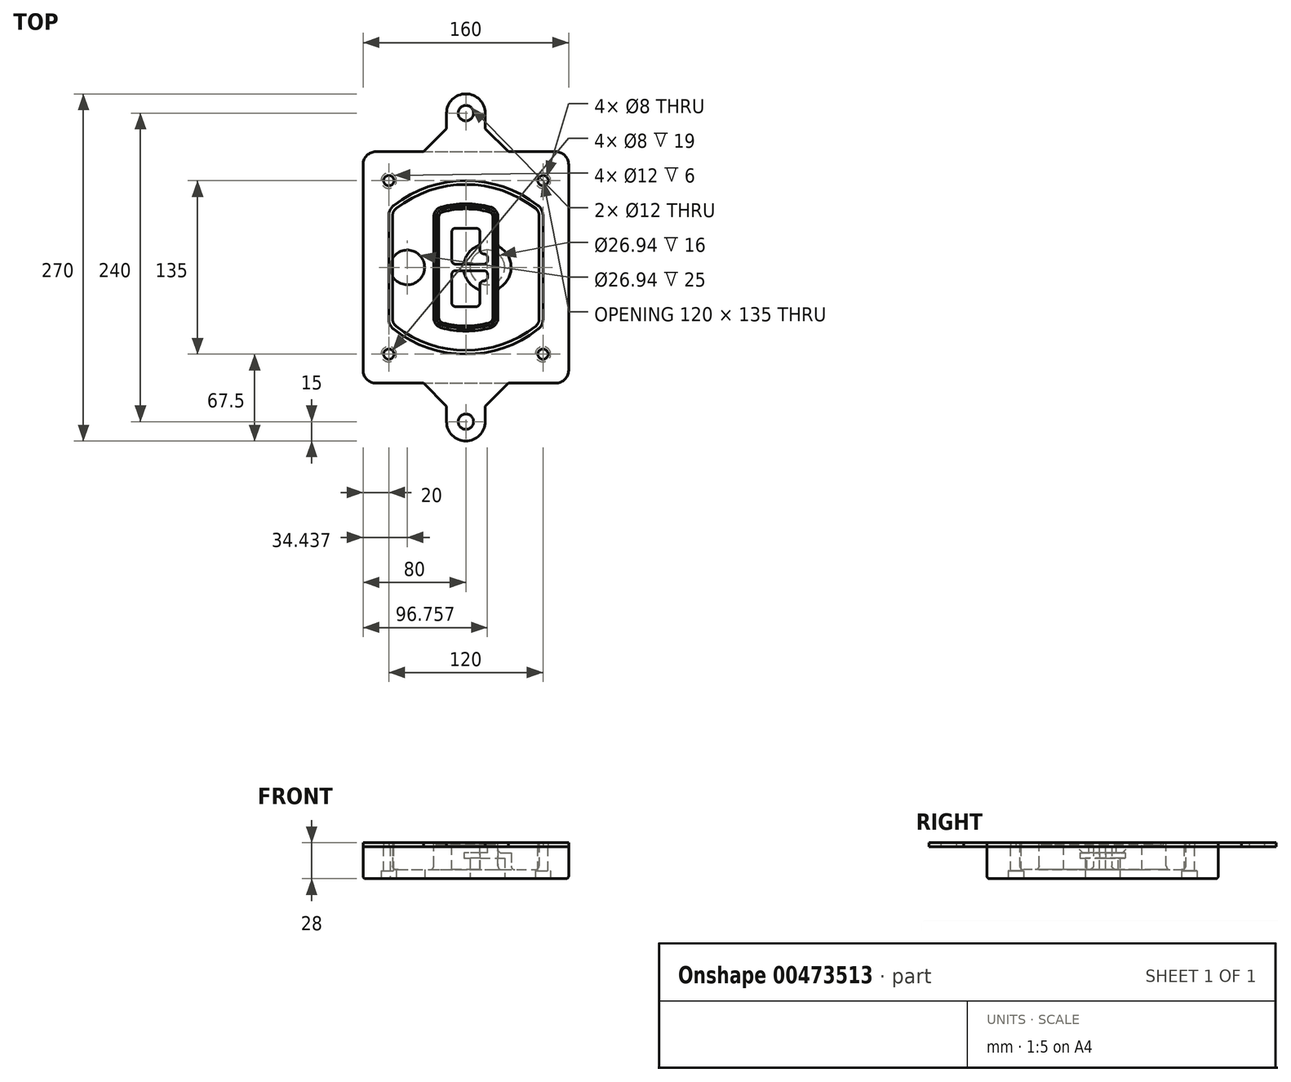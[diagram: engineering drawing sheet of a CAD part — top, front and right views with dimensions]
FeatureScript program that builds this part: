
annotation { "Feature Type Name" : "Feature", "Feature Type Description" : "" }
export const myFeature = defineFeature(function(context is Context, id is Id, definition is map)
    precondition{}
    {
        {
            var Q0;
            Q0=qCreatedBy(makeId("Top.planeOp"),FACE);
            var sketch = newSketch(context, id + "F0", { "sketchPlane" : qUnion([Q0])});
            skPoint(sketch, "E0.rect.middle", {"position": v(0, 0) * mm});
            skLineSegment(sketch, "E1.bottom", {"start": v(-70, -90) * mm, "end": v(70, -90) * mm});
            skLineSegment(sketch, "E1.top", {"start": v(-70, 90) * mm, "end": v(70, 90) * mm});
            skLineSegment(sketch, "E1.left", {"start": v(-80, -80) * mm, "end": v(-80, 80) * mm});
            skLineSegment(sketch, "E1.right", {"start": v(80, -80) * mm, "end": v(80, 80) * mm});
            skLineSegment(sketch, "E2", {"start": v(-80, 90) * mm, "end": v(80, -90) * mm, "construction": true});
            skLineSegment(sketch, "E3", {"start": v(80, 90) * mm, "end": v(-80, -90) * mm, "construction": true});
            skCircle(sketch, "E4", {"center": v(-60, 67.5) * mm, "radius": 4 * mm});
            skCircle(sketch, "E5", {"center": v(60, 67.5) * mm, "radius": 4 * mm});
            skCircle(sketch, "E6", {"center": v(60, -67.5) * mm, "radius": 4 * mm});
            skCircle(sketch, "E7", {"center": v(-60, -67.5) * mm, "radius": 4 * mm});
            skLineSegment(sketch, "E8", {"start": v(-60, 67.5) * mm, "end": v(60, 67.5) * mm, "construction": true});
            skLineSegment(sketch, "E9", {"start": v(60, 67.5) * mm, "end": v(60, -67.5) * mm, "construction": true});
            skLineSegment(sketch, "E10", {"start": v(60, -67.5) * mm, "end": v(-60, -67.5) * mm, "construction": true});
            skLineSegment(sketch, "E11", {"start": v(-60, -67.5) * mm, "end": v(-60, 67.5) * mm, "construction": true});
            skLineSegment(sketch, "E12", {"start": v(-60, 40.3) * mm, "end": v(-60, -40.3) * mm});
            skLineSegment(sketch, "E13", {"start": v(60, 40.3) * mm, "end": v(60, -40.3) * mm});
            skArc(sketch, "E14", {"start": v(56.15, 48.18) * mm, "mid": v(0, 67.5) * mm, "end": v(-56.15, 48.18) * mm});
            skArc(sketch, "E15", {"start": v(-56.15, -48.18) * mm, "mid": v(0, -67.5) * mm, "end": v(56.15, -48.18) * mm});
            skLineSegment(sketch, "E16", {"start": v(-60, 0) * mm, "end": v(60, 0) * mm, "construction": true});
            skPoint(sketch, "E17.visualSharp", {"position": v(-60, -45) * mm});
            skArc(sketch, "E17.filletArc", {"start": v(-60, -40.3) * mm, "mid": v(-58.99, -44.68) * mm, "end": v(-56.15, -48.18) * mm});
            skPoint(sketch, "E18.visualSharp", {"position": v(-60, 45) * mm});
            skArc(sketch, "E18.filletArc", {"start": v(-56.15, 48.18) * mm, "mid": v(-58.99, 44.68) * mm, "end": v(-60, 40.3) * mm});
            skPoint(sketch, "E19.visualSharp", {"position": v(60, 45) * mm});
            skArc(sketch, "E19.filletArc", {"start": v(60, 40.3) * mm, "mid": v(58.99, 44.68) * mm, "end": v(56.15, 48.18) * mm});
            skPoint(sketch, "E20.visualSharp", {"position": v(60, -45) * mm});
            skArc(sketch, "E20.filletArc", {"start": v(56.15, -48.18) * mm, "mid": v(58.99, -44.68) * mm, "end": v(60, -40.3) * mm});
            skPoint(sketch, "E21.visualSharp", {"position": v(-80, 90) * mm});
            skArc(sketch, "E21.filletArc", {"start": v(-70, 90) * mm, "mid": v(-77.07, 87.07) * mm, "end": v(-80, 80) * mm});
            skPoint(sketch, "E22.visualSharp", {"position": v(80, 90) * mm});
            skArc(sketch, "E22.filletArc", {"start": v(80, 80) * mm, "mid": v(77.07, 87.07) * mm, "end": v(70, 90) * mm});
            skPoint(sketch, "E23.visualSharp", {"position": v(80, -90) * mm});
            skArc(sketch, "E23.filletArc", {"start": v(70, -90) * mm, "mid": v(77.07, -87.07) * mm, "end": v(80, -80) * mm});
            skPoint(sketch, "E24.visualSharp", {"position": v(-80, -90) * mm});
            skArc(sketch, "E24.filletArc", {"start": v(-80, -80) * mm, "mid": v(-77.07, -87.07) * mm, "end": v(-70, -90) * mm});
            skArc(sketch, "E25.0", {"start": v(57, 40.3) * mm, "mid": v(56.3, 43.36) * mm, "end": v(54.3, 45.81) * mm});
            skLineSegment(sketch, "E25.1", {"start": v(57, 40.3) * mm, "end": v(57, -40.3) * mm});
            skArc(sketch, "E25.2", {"start": v(54.3, -45.81) * mm, "mid": v(56.3, -43.36) * mm, "end": v(57, -40.3) * mm});
            skArc(sketch, "E25.3", {"start": v(-54.3, -45.81) * mm, "mid": v(0, -64.5) * mm, "end": v(54.3, -45.81) * mm});
            skArc(sketch, "E25.4", {"start": v(-57, -40.3) * mm, "mid": v(-56.3, -43.36) * mm, "end": v(-54.3, -45.81) * mm});
            skArc(sketch, "E25.5", {"start": v(54.3, 45.81) * mm, "mid": v(0, 64.5) * mm, "end": v(-54.3, 45.81) * mm});
            skLineSegment(sketch, "E25.6", {"start": v(-57, 40.3) * mm, "end": v(-57, -40.3) * mm});
            skArc(sketch, "E25.7", {"start": v(-54.3, 45.81) * mm, "mid": v(-56.3, 43.36) * mm, "end": v(-57, 40.3) * mm});
            skArc(sketch, "E26.0", {"start": v(-58.62, 51.33) * mm, "mid": v(-62.58, 46.43) * mm, "end": v(-64, 40.3) * mm});
            skArc(sketch, "E26.1", {"start": v(58.62, 51.33) * mm, "mid": v(0, 71.5) * mm, "end": v(-58.62, 51.33) * mm});
            skArc(sketch, "E26.2", {"start": v(64, 40.3) * mm, "mid": v(62.58, 46.43) * mm, "end": v(58.62, 51.33) * mm});
            skLineSegment(sketch, "E26.3", {"start": v(64, 40.3) * mm, "end": v(64, -40.3) * mm});
            skArc(sketch, "E26.4", {"start": v(58.62, -51.33) * mm, "mid": v(62.58, -46.43) * mm, "end": v(64, -40.3) * mm});
            skLineSegment(sketch, "E26.5", {"start": v(-64, 40.3) * mm, "end": v(-64, -40.3) * mm});
            skArc(sketch, "E26.6", {"start": v(-58.62, -51.33) * mm, "mid": v(0, -71.5) * mm, "end": v(58.62, -51.33) * mm});
            skArc(sketch, "E26.7", {"start": v(-64, -40.3) * mm, "mid": v(-62.58, -46.43) * mm, "end": v(-58.62, -51.33) * mm});
            skSolve(sketch);
        }
        {
            var Q0;
            Q0=makeQuery(id+"F0.imprint","IMPRINT",FACE,{"disambiguationData":[TD([[makeQuery(id+"F0.imprint","IMPRINT",EDGE,{"derivedFrom":sQuery(id+"F0.wireOp",EDGE,"E1.bottom")}),1.0]])]});
            var Q1;
            Q1=makeQuery(id+"F0.imprint","IMPRINT",FACE,{"disambiguationData":[TD([[makeQuery(id+"F0.imprint","IMPRINT",EDGE,{"derivedFrom":sQuery(id+"F0.wireOp",EDGE,"E12")}),1.0]])]});
            var Q2;
            Q2=makeQuery(id+"F0.imprint","IMPRINT",FACE,{"disambiguationData":[TD([[makeQuery(id+"F0.imprint","IMPRINT",EDGE,{"derivedFrom":sQuery(id+"F0.wireOp",EDGE,"E25.0")}),1.0]])]});
            var Q3;
            Q3=makeQuery(id+"F0.imprint","IMPRINT",FACE,{"disambiguationData":[TD([[makeQuery(id+"F0.imprint","IMPRINT",EDGE,{"derivedFrom":sQuery(id+"F0.wireOp",EDGE,"E12")}),-1.0]])]});
            extrude(context, id + "F1", {"entities" : qUnion([Q0, Q1, Q2, Q3]), "oppositeDirection" : true, "depth" : 25 * mm});
        }
        {
            var Q0;
            Q0=makeQuery(id+"F0.imprint","IMPRINT",FACE,{"disambiguationData":[TD([[makeQuery(id+"F0.imprint","IMPRINT",EDGE,{"derivedFrom":sQuery(id+"F0.wireOp",EDGE,"E12")}),1.0]])]});
            extrude(context, id + "F2", {"entities" : qUnion([Q0]), "operationType" : NewBodyOperationType.ADD, "depth" : 3 * mm});
        }
        {
            var Q0;
            Q0=makeQuery(id+"F0.imprint","IMPRINT",FACE,{"disambiguationData":[TD([[makeQuery(id+"F0.imprint","IMPRINT",EDGE,{"derivedFrom":sQuery(id+"F0.wireOp",EDGE,"E25.0")}),1.0]])]});
            extrude(context, id + "F3", {"entities" : qUnion([Q0]), "operationType" : NewBodyOperationType.REMOVE, "oppositeDirection" : true, "depth" : 18 * mm});
        }
        {
            var Q0;
            Q0=makeQuery(id+"F2.opExtrude","CAP_FACE",FACE,{"disambiguationData":[OSD([sQuery(id+"F0.wireOp",EDGE,"E12"),sQuery(id+"F0.wireOp",EDGE,"E13"),sQuery(id+"F0.wireOp",EDGE,"E14"),sQuery(id+"F0.wireOp",EDGE,"E15"),sQuery(id+"F0.wireOp",EDGE,"E17.filletArc"),sQuery(id+"F0.wireOp",EDGE,"E18.filletArc"),sQuery(id+"F0.wireOp",EDGE,"E19.filletArc"),sQuery(id+"F0.wireOp",EDGE,"E20.filletArc"),sQuery(id+"F0.wireOp",EDGE,"E25.0"),sQuery(id+"F0.wireOp",EDGE,"E25.1"),sQuery(id+"F0.wireOp",EDGE,"E25.2"),sQuery(id+"F0.wireOp",EDGE,"E25.3"),sQuery(id+"F0.wireOp",EDGE,"E25.4"),sQuery(id+"F0.wireOp",EDGE,"E25.5"),sQuery(id+"F0.wireOp",EDGE,"E25.6"),sQuery(id+"F0.wireOp",EDGE,"E25.7")])],"isStart":false});
            var sketch = newSketch(context, id + "F4", { "sketchPlane" : qUnion([Q0])});
            skArc(sketch, "E27.0", {"start": v(-19.08, -46.97) * mm, "mid": v(0, -49.5) * mm, "end": v(19.08, -46.97) * mm});
            skArc(sketch, "E28.0", {"start": v(19.08, 46.97) * mm, "mid": v(0, 49.5) * mm, "end": v(-19.08, 46.97) * mm});
            skLineSegment(sketch, "E29", {"start": v(-25, 39.25) * mm, "end": v(-25, -39.25) * mm});
            skLineSegment(sketch, "E30", {"start": v(25, 39.25) * mm, "end": v(25, -39.25) * mm});
            skLineSegment(sketch, "E31", {"start": v(-25, 45.1) * mm, "end": v(25, 45.1) * mm, "construction": true});
            skLineSegment(sketch, "E32", {"start": v(-25, -45.1) * mm, "end": v(25, -45.1) * mm, "construction": true});
            skPoint(sketch, "E33.visualSharp", {"position": v(-25, 45.1) * mm});
            skArc(sketch, "E33.filletArc", {"start": v(-19.08, 46.97) * mm, "mid": v(-23.35, 44.11) * mm, "end": v(-25, 39.25) * mm});
            skPoint(sketch, "E34.visualSharp", {"position": v(25, 45.1) * mm});
            skArc(sketch, "E34.filletArc", {"start": v(25, 39.25) * mm, "mid": v(23.35, 44.11) * mm, "end": v(19.08, 46.97) * mm});
            skPoint(sketch, "E35.visualSharp", {"position": v(25, -45.1) * mm});
            skArc(sketch, "E35.filletArc", {"start": v(19.08, -46.97) * mm, "mid": v(23.35, -44.11) * mm, "end": v(25, -39.25) * mm});
            skPoint(sketch, "E36.visualSharp", {"position": v(-25, -45.1) * mm});
            skArc(sketch, "E36.filletArc", {"start": v(-25, -39.25) * mm, "mid": v(-23.35, -44.11) * mm, "end": v(-19.08, -46.97) * mm});
            skArc(sketch, "E37.0", {"start": v(54.3, 45.81) * mm, "mid": v(0, 64.5) * mm, "end": v(-54.3, 45.81) * mm});
            skArc(sketch, "E37.1", {"start": v(-54.3, 45.81) * mm, "mid": v(-56.3, 43.36) * mm, "end": v(-57, 40.3) * mm});
            skLineSegment(sketch, "E37.2", {"start": v(-57, 40.3) * mm, "end": v(-57, -40.3) * mm});
            skArc(sketch, "E37.3", {"start": v(-57, -40.3) * mm, "mid": v(-56.3, -43.36) * mm, "end": v(-54.3, -45.81) * mm});
            skArc(sketch, "E37.4", {"start": v(-54.3, -45.81) * mm, "mid": v(0, -64.5) * mm, "end": v(54.3, -45.81) * mm});
            skArc(sketch, "E37.5", {"start": v(54.3, -45.81) * mm, "mid": v(56.3, -43.36) * mm, "end": v(57, -40.3) * mm});
            skLineSegment(sketch, "E37.6", {"start": v(57, 40.3) * mm, "end": v(57, -40.3) * mm});
            skArc(sketch, "E37.7", {"start": v(57, 40.3) * mm, "mid": v(56.3, 43.36) * mm, "end": v(54.3, 45.81) * mm});
            skLineSegment(sketch, "E38.0", {"start": v(23, 39.25) * mm, "end": v(23, -39.25) * mm});
            skArc(sketch, "E38.1", {"start": v(18.56, -45.04) * mm, "mid": v(21.76, -42.9) * mm, "end": v(23, -39.25) * mm});
            skArc(sketch, "E38.2", {"start": v(-18.56, -45.04) * mm, "mid": v(0, -47.5) * mm, "end": v(18.56, -45.04) * mm});
            skArc(sketch, "E38.3", {"start": v(-23, -39.25) * mm, "mid": v(-21.76, -42.9) * mm, "end": v(-18.56, -45.04) * mm});
            skLineSegment(sketch, "E38.4", {"start": v(-23, 39.25) * mm, "end": v(-23, -39.25) * mm});
            skArc(sketch, "E38.5", {"start": v(23, 39.25) * mm, "mid": v(21.76, 42.9) * mm, "end": v(18.56, 45.04) * mm});
            skArc(sketch, "E38.6", {"start": v(-18.56, 45.04) * mm, "mid": v(-21.76, 42.9) * mm, "end": v(-23, 39.25) * mm});
            skArc(sketch, "E38.7", {"start": v(18.56, 45.04) * mm, "mid": v(0, 47.5) * mm, "end": v(-18.56, 45.04) * mm});
            skArc(sketch, "E39.0", {"start": v(21, 39.25) * mm, "mid": v(20.18, 41.68) * mm, "end": v(18.04, 43.1) * mm});
            skLineSegment(sketch, "E39.1", {"start": v(21, 39.25) * mm, "end": v(21, -39.25) * mm});
            skArc(sketch, "E39.2", {"start": v(18.04, -43.1) * mm, "mid": v(20.18, -41.68) * mm, "end": v(21, -39.25) * mm});
            skArc(sketch, "E39.3", {"start": v(-18.04, -43.1) * mm, "mid": v(0, -45.5) * mm, "end": v(18.04, -43.1) * mm});
            skArc(sketch, "E39.4", {"start": v(-21, -39.25) * mm, "mid": v(-20.18, -41.68) * mm, "end": v(-18.04, -43.1) * mm});
            skArc(sketch, "E39.5", {"start": v(18.04, 43.1) * mm, "mid": v(0, 45.5) * mm, "end": v(-18.04, 43.1) * mm});
            skLineSegment(sketch, "E39.6", {"start": v(-21, 39.25) * mm, "end": v(-21, -39.25) * mm});
            skArc(sketch, "E39.7", {"start": v(-18.04, 43.1) * mm, "mid": v(-20.18, 41.68) * mm, "end": v(-21, 39.25) * mm});
            skLineSegment(sketch, "E40", {"start": v(-25, 0) * mm, "end": v(25, 0) * mm, "construction": true});
            skLineSegment(sketch, "E41", {"start": v(-11, 5.5) * mm, "end": v(-11, 27.5) * mm});
            skLineSegment(sketch, "E42", {"start": v(-8, 30.5) * mm, "end": v(8, 30.5) * mm});
            skLineSegment(sketch, "E43", {"start": v(11, 27.5) * mm, "end": v(11, 13.5) * mm});
            skLineSegment(sketch, "E44", {"start": v(14, 10.5) * mm, "end": v(14, 10.5) * mm});
            skLineSegment(sketch, "E45", {"start": v(17, 7.5) * mm, "end": v(17, 5.5) * mm});
            skLineSegment(sketch, "E46", {"start": v(14, 2.5) * mm, "end": v(-8, 2.5) * mm});
            skPoint(sketch, "E47.visualSharp", {"position": v(-11, 30.5) * mm});
            skArc(sketch, "E47.filletArc", {"start": v(-8, 30.5) * mm, "mid": v(-10.12, 29.62) * mm, "end": v(-11, 27.5) * mm});
            skPoint(sketch, "E48.visualSharp", {"position": v(11, 30.5) * mm});
            skArc(sketch, "E48.filletArc", {"start": v(11, 27.5) * mm, "mid": v(10.12, 29.62) * mm, "end": v(8, 30.5) * mm});
            skPoint(sketch, "E49.visualSharp", {"position": v(11, 10.5) * mm});
            skArc(sketch, "E49.filletArc", {"start": v(11, 13.5) * mm, "mid": v(11.88, 11.38) * mm, "end": v(14, 10.5) * mm});
            skPoint(sketch, "E50.visualSharp", {"position": v(17, 10.5) * mm});
            skArc(sketch, "E50.filletArc", {"start": v(17, 7.5) * mm, "mid": v(16.12, 9.62) * mm, "end": v(14, 10.5) * mm});
            skPoint(sketch, "E51.visualSharp", {"position": v(17, 2.5) * mm});
            skArc(sketch, "E51.filletArc", {"start": v(14, 2.5) * mm, "mid": v(16.12, 3.38) * mm, "end": v(17, 5.5) * mm});
            skPoint(sketch, "E52.visualSharp", {"position": v(-11, 2.5) * mm});
            skArc(sketch, "E52.filletArc", {"start": v(-11, 5.5) * mm, "mid": v(-10.12, 3.38) * mm, "end": v(-8, 2.5) * mm});
            skLineSegment(sketch, "E53.0.MirrorCS", {"start": v(14, -2.5) * mm, "end": v(-8, -2.5) * mm});
            skArc(sketch, "E54.0.MirrorCS", {"start": v(-11, -5.5) * mm, "mid": v(-10.12, -3.38) * mm, "end": v(-8, -2.5) * mm});
            skLineSegment(sketch, "E55.0.MirrorCS", {"start": v(-11, -5.5) * mm, "end": v(-11, -27.5) * mm});
            skArc(sketch, "E56.0.MirrorCS", {"start": v(-8, -30.5) * mm, "mid": v(-10.12, -29.62) * mm, "end": v(-11, -27.5) * mm});
            skLineSegment(sketch, "E57.0.MirrorCS", {"start": v(-8, -30.5) * mm, "end": v(8, -30.5) * mm});
            skArc(sketch, "E58.0.MirrorCS", {"start": v(11, -27.5) * mm, "mid": v(10.12, -29.62) * mm, "end": v(8, -30.5) * mm});
            skLineSegment(sketch, "E59.0.MirrorCS", {"start": v(11, -27.5) * mm, "end": v(11, -13.5) * mm});
            skArc(sketch, "E60.0.MirrorCS", {"start": v(11, -13.5) * mm, "mid": v(11.88, -11.38) * mm, "end": v(14, -10.5) * mm});
            skArc(sketch, "E61.0.MirrorCS", {"start": v(17, -7.5) * mm, "mid": v(16.12, -9.62) * mm, "end": v(14, -10.5) * mm});
            skLineSegment(sketch, "E62.0.MirrorCS", {"start": v(17, -7.5) * mm, "end": v(17, -5.5) * mm});
            skArc(sketch, "E63.0.MirrorCS", {"start": v(14, -2.5) * mm, "mid": v(16.12, -3.38) * mm, "end": v(17, -5.5) * mm});
            skSolve(sketch);
        }
        {
            var Q0;
            Q0=makeQuery(id+"F4.imprint","IMPRINT",FACE,{"disambiguationData":[TD([[makeQuery(id+"F4.imprint","IMPRINT",EDGE,{"derivedFrom":sQuery(id+"F4.wireOp",EDGE,"E27.0")}),1.0]])]});
            var Q1;
            Q1=makeQuery(id+"F4.imprint","IMPRINT",FACE,{"disambiguationData":[TD([[makeQuery(id+"F4.imprint","IMPRINT",EDGE,{"derivedFrom":sQuery(id+"F4.wireOp",EDGE,"E38.0")}),-1.0]])]});
            var Q2;
            Q2=makeQuery(id+"F4.imprint","IMPRINT",FACE,{"disambiguationData":[TD([[makeQuery(id+"F4.imprint","IMPRINT",EDGE,{"derivedFrom":sQuery(id+"F4.wireOp",EDGE,"E39.0")}),1.0]])]});
            extrude(context, id + "F5", {"entities" : qUnion([Q0, Q1, Q2]), "operationType" : NewBodyOperationType.ADD, "endBound" : BoundingType.UP_TO_NEXT, "oppositeDirection" : true, "depth" : 25 * mm});
        }
        {
            var Q0;
            Q0=makeQuery(id+"F4.imprint","IMPRINT",FACE,{"disambiguationData":[TD([[makeQuery(id+"F4.imprint","IMPRINT",EDGE,{"derivedFrom":sQuery(id+"F4.wireOp",EDGE,"E38.0")}),-1.0]])]});
            extrude(context, id + "F6", {"entities" : qUnion([Q0]), "operationType" : NewBodyOperationType.REMOVE, "oppositeDirection" : true, "depth" : 2 * mm});
        }
        {
            var Q0;
            Q0=makeQuery(id+"F1.opExtrude","CAP_FACE",FACE,{"disambiguationData":[OSD([sQuery(id+"F0.wireOp",EDGE,"E1.bottom"),sQuery(id+"F0.wireOp",EDGE,"E1.top"),sQuery(id+"F0.wireOp",EDGE,"E1.left"),sQuery(id+"F0.wireOp",EDGE,"E1.right"),sQuery(id+"F0.wireOp",EDGE,"E4"),sQuery(id+"F0.wireOp",EDGE,"E5"),sQuery(id+"F0.wireOp",EDGE,"E6"),sQuery(id+"F0.wireOp",EDGE,"E7"),sQuery(id+"F0.wireOp",EDGE,"E21.filletArc"),sQuery(id+"F0.wireOp",EDGE,"E22.filletArc"),sQuery(id+"F0.wireOp",EDGE,"E23.filletArc"),sQuery(id+"F0.wireOp",EDGE,"E24.filletArc")])],"isStart":false});
            var sketch = newSketch(context, id + "F7", { "sketchPlane" : qUnion([Q0])});
            skCircle(sketch, "E64", {"center": v(16.76, 0) * mm, "radius": 13.47 * mm});
            skCircle(sketch, "E65", {"center": v(-45.56, 0) * mm, "radius": 13.47 * mm});
            skLineSegment(sketch, "E66", {"start": v(80, 0) * mm, "end": v(-80, 0) * mm});
            skCircle(sketch, "E67", {"center": v(16.76, 0) * mm, "radius": 18.47 * mm});
            skCircle(sketch, "E68", {"center": v(60, -67.5) * mm, "radius": 6 * mm});
            skCircle(sketch, "E69", {"center": v(-60, -67.5) * mm, "radius": 6 * mm});
            skCircle(sketch, "E70", {"center": v(-60, 67.5) * mm, "radius": 6 * mm});
            skCircle(sketch, "E71", {"center": v(60, 67.5) * mm, "radius": 6 * mm});
            skSolve(sketch);
        }
        {
            var Q0;
            {var subQ1=sQuery(id+"F7.wireOp",EDGE,"E66");var subQ4=sQuery(id+"F7.wireOp",EDGE,"E64");var subQ6=makeQuery(id+"F7.imprint","INTERSECT",VERTEX,{"disambiguationData":[OD(0.0)],"derivedFrom":[subQ4,subQ1]});Q0=makeQuery(id+"F7.imprint","IMPRINT",FACE,{"disambiguationData":[TD([[makeQuery(id+"F7.imprint","IMPRINT",EDGE,{"disambiguationData":[TD([[subQ6,-1.0]])],"derivedFrom":subQ4}),-1.0]])]});}
            var Q1;
            {var subQ0=sQuery(id+"F7.wireOp",EDGE,"E66");var subQ1=sQuery(id+"F7.wireOp",EDGE,"E64");var subQ3=makeQuery(id+"F7.imprint","INTERSECT",VERTEX,{"disambiguationData":[OD(0.0)],"derivedFrom":[subQ1,subQ0]});Q1=makeQuery(id+"F7.imprint","IMPRINT",FACE,{"disambiguationData":[TD([[makeQuery(id+"F7.imprint","IMPRINT",EDGE,{"disambiguationData":[TD([[subQ3,-1.0]])],"derivedFrom":subQ1}),1.0]])]});}
            var Q2;
            {var subQ0=sQuery(id+"F7.wireOp",EDGE,"E66");var subQ1=sQuery(id+"F7.wireOp",EDGE,"E64");var subQ3=makeQuery(id+"F7.imprint","INTERSECT",VERTEX,{"disambiguationData":[OD(0.0)],"derivedFrom":[subQ1,subQ0]});Q2=makeQuery(id+"F7.imprint","IMPRINT",FACE,{"disambiguationData":[TD([[makeQuery(id+"F7.imprint","IMPRINT",EDGE,{"disambiguationData":[TD([[subQ3,1.0]])],"derivedFrom":subQ1}),1.0]])]});}
            var Q3;
            {var subQ1=sQuery(id+"F7.wireOp",EDGE,"E66");var subQ4=sQuery(id+"F7.wireOp",EDGE,"E64");var subQ6=makeQuery(id+"F7.imprint","INTERSECT",VERTEX,{"disambiguationData":[OD(0.0)],"derivedFrom":[subQ4,subQ1]});Q3=makeQuery(id+"F7.imprint","IMPRINT",FACE,{"disambiguationData":[TD([[makeQuery(id+"F7.imprint","IMPRINT",EDGE,{"disambiguationData":[TD([[subQ6,1.0]])],"derivedFrom":subQ4}),-1.0]])]});}
            extrude(context, id + "F8", {"entities" : qUnion([Q0, Q1, Q2, Q3]), "operationType" : NewBodyOperationType.ADD, "oppositeDirection" : true, "depth" : 20 * mm});
        }
        {
            var Q0;
            {var subQ0=sQuery(id+"F7.wireOp",EDGE,"E66");var subQ1=sQuery(id+"F7.wireOp",EDGE,"E64");var subQ3=makeQuery(id+"F7.imprint","INTERSECT",VERTEX,{"disambiguationData":[OD(0.0)],"derivedFrom":[subQ1,subQ0]});Q0=makeQuery(id+"F7.imprint","IMPRINT",FACE,{"disambiguationData":[TD([[makeQuery(id+"F7.imprint","IMPRINT",EDGE,{"disambiguationData":[TD([[subQ3,-1.0]])],"derivedFrom":subQ1}),1.0]])]});}
            var Q1;
            {var subQ0=sQuery(id+"F7.wireOp",EDGE,"E66");var subQ1=sQuery(id+"F7.wireOp",EDGE,"E64");var subQ3=makeQuery(id+"F7.imprint","INTERSECT",VERTEX,{"disambiguationData":[OD(0.0)],"derivedFrom":[subQ1,subQ0]});Q1=makeQuery(id+"F7.imprint","IMPRINT",FACE,{"disambiguationData":[TD([[makeQuery(id+"F7.imprint","IMPRINT",EDGE,{"disambiguationData":[TD([[subQ3,1.0]])],"derivedFrom":subQ1}),1.0]])]});}
            extrude(context, id + "F9", {"entities" : qUnion([Q0, Q1]), "operationType" : NewBodyOperationType.REMOVE, "oppositeDirection" : true, "depth" : 16 * mm});
        }
        {
            var Q0;
            {var subQ0=sQuery(id+"F7.wireOp",EDGE,"E66");var subQ1=sQuery(id+"F7.wireOp",EDGE,"E65");var subQ3=makeQuery(id+"F7.imprint","INTERSECT",VERTEX,{"disambiguationData":[OD(0.0)],"derivedFrom":[subQ1,subQ0]});Q0=makeQuery(id+"F7.imprint","IMPRINT",FACE,{"disambiguationData":[TD([[makeQuery(id+"F7.imprint","IMPRINT",EDGE,{"disambiguationData":[TD([[subQ3,-1.0]])],"derivedFrom":subQ1}),1.0]])]});}
            var Q1;
            {var subQ0=sQuery(id+"F7.wireOp",EDGE,"E66");var subQ1=sQuery(id+"F7.wireOp",EDGE,"E65");var subQ3=makeQuery(id+"F7.imprint","INTERSECT",VERTEX,{"disambiguationData":[OD(0.0)],"derivedFrom":[subQ1,subQ0]});Q1=makeQuery(id+"F7.imprint","IMPRINT",FACE,{"disambiguationData":[TD([[makeQuery(id+"F7.imprint","IMPRINT",EDGE,{"disambiguationData":[TD([[subQ3,1.0]])],"derivedFrom":subQ1}),1.0]])]});}
            extrude(context, id + "F10", {"entities" : qUnion([Q0, Q1]), "operationType" : NewBodyOperationType.REMOVE, "oppositeDirection" : true, "depth" : 25 * mm});
        }
        {
            var Q0;
            Q0=makeQuery(id+"F7.imprint","IMPRINT",FACE,{"disambiguationData":[TD([[makeQuery(id+"F7.imprint","IMPRINT",EDGE,{"derivedFrom":sQuery(id+"F7.wireOp",EDGE,"E68")}),1.0]])]});
            var Q1;
            Q1=makeQuery(id+"F7.imprint","IMPRINT",FACE,{"disambiguationData":[TD([[makeQuery(id+"F7.imprint","IMPRINT",EDGE,{"derivedFrom":makeQuery(id+"F1.opExtrude","CAP_EDGE",EDGE,{"disambiguationData":[OSD([sQuery(id+"F0.wireOp",EDGE,"E5")])],"isStart":false})}),-1.0]])]});
            var Q2;
            Q2=makeQuery(id+"F7.imprint","IMPRINT",FACE,{"disambiguationData":[TD([[makeQuery(id+"F7.imprint","IMPRINT",EDGE,{"derivedFrom":sQuery(id+"F7.wireOp",EDGE,"E69")}),1.0]])]});
            var Q3;
            Q3=makeQuery(id+"F7.imprint","IMPRINT",FACE,{"disambiguationData":[TD([[makeQuery(id+"F7.imprint","IMPRINT",EDGE,{"derivedFrom":makeQuery(id+"F1.opExtrude","CAP_EDGE",EDGE,{"disambiguationData":[OSD([sQuery(id+"F0.wireOp",EDGE,"E4")])],"isStart":false})}),-1.0]])]});
            var Q4;
            Q4=makeQuery(id+"F7.imprint","IMPRINT",FACE,{"disambiguationData":[TD([[makeQuery(id+"F7.imprint","IMPRINT",EDGE,{"derivedFrom":sQuery(id+"F7.wireOp",EDGE,"E70")}),1.0]])]});
            var Q5;
            Q5=makeQuery(id+"F7.imprint","IMPRINT",FACE,{"disambiguationData":[TD([[makeQuery(id+"F7.imprint","IMPRINT",EDGE,{"derivedFrom":makeQuery(id+"F1.opExtrude","CAP_EDGE",EDGE,{"disambiguationData":[OSD([sQuery(id+"F0.wireOp",EDGE,"E7")])],"isStart":false})}),-1.0]])]});
            var Q6;
            Q6=makeQuery(id+"F7.imprint","IMPRINT",FACE,{"disambiguationData":[TD([[makeQuery(id+"F7.imprint","IMPRINT",EDGE,{"derivedFrom":sQuery(id+"F7.wireOp",EDGE,"E71")}),1.0]])]});
            var Q7;
            Q7=makeQuery(id+"F7.imprint","IMPRINT",FACE,{"disambiguationData":[TD([[makeQuery(id+"F7.imprint","IMPRINT",EDGE,{"derivedFrom":makeQuery(id+"F1.opExtrude","CAP_EDGE",EDGE,{"disambiguationData":[OSD([sQuery(id+"F0.wireOp",EDGE,"E6")])],"isStart":false})}),-1.0]])]});
            extrude(context, id + "F11", {"entities" : qUnion([Q0, Q1, Q2, Q3, Q4, Q5, Q6, Q7]), "operationType" : NewBodyOperationType.REMOVE, "oppositeDirection" : true, "depth" : 6 * mm});
        }
        {
            var Q0;
            Q0=makeQuery(id+"F9.boolean.opBoolean","COPY",FACE,{"derivedFrom":makeQuery(id+"F9.opExtrude","CAP_FACE",FACE,{"disambiguationData":[OSD([sQuery(id+"F7.wireOp",EDGE,"E64")])],"isStart":false})});
            var sketch = newSketch(context, id + "F12", { "sketchPlane" : qUnion([Q0])});
            skArc(sketch, "E72.0", {"start": v(11, 17.55) * mm, "mid": v(2.57, 11.82) * mm, "end": v(-1.54, 2.5) * mm});
            skArc(sketch, "E72.1", {"start": v(-1.54, -2.5) * mm, "mid": v(2.57, -11.82) * mm, "end": v(11, -17.55) * mm});
            skLineSegment(sketch, "E73", {"start": v(-1.54, -2.5) * mm, "end": v(14, -2.5) * mm});
            skLineSegment(sketch, "E74.0", {"start": v(14, 2.5) * mm, "end": v(-1.54, 2.5) * mm});
            skArc(sketch, "E74.1", {"start": v(14, 2.5) * mm, "mid": v(16.12, 3.38) * mm, "end": v(17, 5.5) * mm});
            skLineSegment(sketch, "E74.2", {"start": v(17, 7.5) * mm, "end": v(17, 5.5) * mm});
            skArc(sketch, "E74.3", {"start": v(17, 7.5) * mm, "mid": v(16.12, 9.62) * mm, "end": v(14, 10.5) * mm});
            skArc(sketch, "E74.4", {"start": v(11, 13.5) * mm, "mid": v(11.88, 11.38) * mm, "end": v(14, 10.5) * mm});
            skLineSegment(sketch, "E74.5", {"start": v(11, 17.55) * mm, "end": v(11, 13.5) * mm});
            skLineSegment(sketch, "E74.7", {"start": v(14, -2.5) * mm, "end": v(-1.54, -2.5) * mm});
            skArc(sketch, "E74.8", {"start": v(14, -2.5) * mm, "mid": v(16.12, -3.38) * mm, "end": v(17, -5.5) * mm});
            skLineSegment(sketch, "E74.9", {"start": v(17, -7.5) * mm, "end": v(17, -5.5) * mm});
            skArc(sketch, "E74.10", {"start": v(17, -7.5) * mm, "mid": v(16.12, -9.62) * mm, "end": v(14, -10.5) * mm});
            skArc(sketch, "E74.11", {"start": v(11, -13.5) * mm, "mid": v(11.88, -11.38) * mm, "end": v(14, -10.5) * mm});
            skLineSegment(sketch, "E74.12", {"start": v(11, -17.55) * mm, "end": v(11, -13.5) * mm});
            skPoint(sketch, "E75.orphan", {"position": v(11, -27.5) * mm});
            skPoint(sketch, "E76.orphan", {"position": v(-8, -2.5) * mm});
            skPoint(sketch, "E77.orphan", {"position": v(-8, 2.5) * mm});
            skPoint(sketch, "E78.orphan", {"position": v(11, 27.5) * mm});
            skSolve(sketch);
        }
        {
            var Q0;
            {var subQ7=sQuery(id+"F12.wireOp",EDGE,"E72.0");var subQ14=sQuery(id+"F12.wireOp",EDGE,"E72.1");var subQ16=sQuery(id+"F12.wireOp",EDGE,"E74.1");var subQ18=sQuery(id+"F12.wireOp",EDGE,"E74.8");Q0=qUnion([makeQuery(id+"F12.imprint","IMPRINT",FACE,{"disambiguationData":[TD([[makeQuery(id+"F12.imprint","IMPRINT",EDGE,{"derivedFrom":subQ7}),1.0]])]}),makeQuery(id+"F12.imprint","IMPRINT",FACE,{"disambiguationData":[TD([[makeQuery(id+"F12.imprint","IMPRINT",EDGE,{"derivedFrom":subQ14}),1.0]])]}),makeQuery(id+"F12.imprint","IMPRINT",FACE,{"disambiguationData":[TD([[makeQuery(id+"F12.imprint","IMPRINT",EDGE,{"derivedFrom":subQ16}),1.0]])]}),makeQuery(id+"F12.imprint","IMPRINT",FACE,{"disambiguationData":[TD([[makeQuery(id+"F12.imprint","IMPRINT",EDGE,{"derivedFrom":subQ18}),-1.0]])]})]);}
            var Q1;
            Q1=makeQuery(id+"F5.boolean.opBoolean","SPLIT",FACE,{"disambiguationData":[TD([makeQuery(id+"F5.opExtrude","SWEPT_FACE",FACE,{"disambiguationData":[OSD([sQuery(id+"F4.wireOp",EDGE,"E41")])]})])],"derivedFrom":makeQuery(id+"F3.boolean.opBoolean","COPY",FACE,{"derivedFrom":makeQuery(id+"F3.opExtrude","CAP_FACE",FACE,{"disambiguationData":[OSD([sQuery(id+"F0.wireOp",EDGE,"E25.0"),sQuery(id+"F0.wireOp",EDGE,"E25.1"),sQuery(id+"F0.wireOp",EDGE,"E25.2"),sQuery(id+"F0.wireOp",EDGE,"E25.3"),sQuery(id+"F0.wireOp",EDGE,"E25.4"),sQuery(id+"F0.wireOp",EDGE,"E25.5"),sQuery(id+"F0.wireOp",EDGE,"E25.6"),sQuery(id+"F0.wireOp",EDGE,"E25.7")])],"isStart":false})})});
            extrude(context, id + "F13", {"entities" : qUnion([Q0]), "operationType" : NewBodyOperationType.REMOVE, "endBound" : BoundingType.UP_TO_SURFACE, "endBoundEntityFace" : qUnion([Q1]), "depth" : 25 * mm});
        }
        {
            var Q0;
            Q0=makeQuery(id+"F3.boolean.opBoolean","COPY",EDGE,{"derivedFrom":makeQuery(id+"F3.opExtrude","CAP_EDGE",EDGE,{"disambiguationData":[OSD([sQuery(id+"F0.wireOp",EDGE,"E25.6")])],"isStart":false})});
            var Q1;
            Q1=makeQuery(id+"F8.boolean.opBoolean","INTERSECT",EDGE,{"derivedFrom":[makeQuery(id+"F5.opExtrude","SWEPT_FACE",FACE,{"disambiguationData":[OSD([sQuery(id+"F4.wireOp",EDGE,"E30")])]}),makeQuery(id+"F8.opExtrude","CAP_FACE",FACE,{"disambiguationData":[OSD([sQuery(id+"F7.wireOp",EDGE,"E67")])],"isStart":false})]});
            var Q2;
            Q2=makeQuery(id+"F8.boolean.opBoolean","INTERSECT",EDGE,{"disambiguationData":[OD(1.0)],"derivedFrom":[makeQuery(id+"F5.opExtrude","SWEPT_FACE",FACE,{"disambiguationData":[OSD([sQuery(id+"F4.wireOp",EDGE,"E30")])]}),makeQuery(id+"F8.opExtrude","SWEPT_FACE",FACE,{"disambiguationData":[OSD([sQuery(id+"F7.wireOp",EDGE,"E67")])]})]});
            var Q3;
            {var subQ0=sQuery(id+"F4.wireOp",EDGE,"E30");Q3=makeQuery(id+"F8.boolean.opBoolean","SPLIT",EDGE,{"disambiguationData":[TD([makeQuery(id+"F5.opExtrude","SWEPT_FACE",FACE,{"disambiguationData":[OSD([sQuery(id+"F4.wireOp",EDGE,"E35.filletArc")])]})])],"derivedFrom":makeQuery(id+"F5.opExtrude","CAP_EDGE",EDGE,{"disambiguationData":[OSD([subQ0])],"isStart":false})});}
            var Q4;
            {var subQ0=sQuery(id+"F0.wireOp",EDGE,"E25.7");var subQ1=sQuery(id+"F0.wireOp",EDGE,"E25.1");var subQ2=sQuery(id+"F0.wireOp",EDGE,"E25.6");var subQ3=sQuery(id+"F0.wireOp",EDGE,"E25.5");var subQ4=sQuery(id+"F0.wireOp",EDGE,"E25.4");var subQ5=sQuery(id+"F0.wireOp",EDGE,"E25.0");var subQ6=sQuery(id+"F0.wireOp",EDGE,"E25.2");var subQ7=sQuery(id+"F0.wireOp",EDGE,"E25.3");Q4=makeQuery(id+"F8.boolean.opBoolean","INTERSECT",EDGE,{"derivedFrom":[makeQuery(id+"F5.boolean.opBoolean","SPLIT",FACE,{"disambiguationData":[TD([makeQuery(id+"F2.opExtrude","SWEPT_FACE",FACE,{"disambiguationData":[OSD([subQ5])]})])],"derivedFrom":makeQuery(id+"F3.boolean.opBoolean","COPY",FACE,{"derivedFrom":makeQuery(id+"F3.opExtrude","CAP_FACE",FACE,{"disambiguationData":[OSD([subQ5,subQ1,subQ6,subQ7,subQ4,subQ3,subQ2,subQ0])],"isStart":false})})}),makeQuery(id+"F8.opExtrude","SWEPT_FACE",FACE,{"disambiguationData":[OSD([sQuery(id+"F7.wireOp",EDGE,"E67")])]})]});}
            var Q5;
            Q5=makeQuery(id+"F8.boolean.opBoolean","INTERSECT",EDGE,{"disambiguationData":[OD(0.0)],"derivedFrom":[makeQuery(id+"F5.opExtrude","SWEPT_FACE",FACE,{"disambiguationData":[OSD([sQuery(id+"F4.wireOp",EDGE,"E30")])]}),makeQuery(id+"F8.opExtrude","SWEPT_FACE",FACE,{"disambiguationData":[OSD([sQuery(id+"F7.wireOp",EDGE,"E67")])]})]});
            fillet(context, id + "F14", {"entities" : qUnion([Q0, Q1, Q2, Q3, Q4, Q5]), "radius" : 3 * mm, "tangentPropagation" : true, "allowEdgeOverflow" : false});
        }
        {
            var Q0;
            Q0=makeQuery(id+"F1.opExtrude","CAP_EDGE",EDGE,{"disambiguationData":[OSD([sQuery(id+"F0.wireOp",EDGE,"E1.bottom")])],"isStart":false});
            fillet(context, id + "F15", {"entities" : qUnion([Q0]), "radius" : 2 * mm, "tangentPropagation" : true, "allowEdgeOverflow" : false});
        }
        {
            var Q0;
            {var subQ0=sQuery(id+"F0.wireOp",EDGE,"E21.filletArc");var subQ1=sQuery(id+"F0.wireOp",EDGE,"E7");var subQ2=sQuery(id+"F0.wireOp",EDGE,"E6");var subQ3=sQuery(id+"F0.wireOp",EDGE,"E5");var subQ4=sQuery(id+"F0.wireOp",EDGE,"E4");var subQ5=sQuery(id+"F0.wireOp",EDGE,"E22.filletArc");var subQ6=sQuery(id+"F0.wireOp",EDGE,"E1.bottom");var subQ7=sQuery(id+"F0.wireOp",EDGE,"E1.right");var subQ8=sQuery(id+"F0.wireOp",EDGE,"E1.top");var subQ9=sQuery(id+"F0.wireOp",EDGE,"E1.left");var subQ10=sQuery(id+"F0.wireOp",EDGE,"E23.filletArc");var subQ11=sQuery(id+"F0.wireOp",EDGE,"E24.filletArc");Q0=makeQuery(id+"F2.boolean.opBoolean","SPLIT",FACE,{"disambiguationData":[TD([makeQuery(id+"F1.opExtrude","SWEPT_FACE",FACE,{"disambiguationData":[OSD([subQ6])]})])],"derivedFrom":makeQuery(id+"F1.opExtrude","CAP_FACE",FACE,{"disambiguationData":[OSD([subQ6,subQ8,subQ9,subQ7,subQ4,subQ3,subQ2,subQ1,subQ0,subQ5,subQ10,subQ11])],"isStart":true})});}
            var sketch = newSketch(context, id + "F16", { "sketchPlane" : qUnion([Q0])});
            skLineSegment(sketch, "E79", {"start": v(0, 90) * mm, "end": v(0, 120) * mm, "construction": true});
            skPoint(sketch, "E79.endSnap0", {"position": v(0, 90) * mm});
            skCircle(sketch, "E80", {"center": v(0, 120) * mm, "radius": 6 * mm});
            skLineSegment(sketch, "E81", {"start": v(33, 90) * mm, "end": v(15, 108) * mm});
            skLineSegment(sketch, "E82", {"start": v(15, 108) * mm, "end": v(15, 120) * mm});
            skArc(sketch, "E83", {"start": v(15, 120) * mm, "mid": v(0, 135) * mm, "end": v(-15, 120) * mm});
            skLineSegment(sketch, "E84", {"start": v(-15, 120) * mm, "end": v(-15, 108) * mm});
            skLineSegment(sketch, "E85", {"start": v(-15, 108) * mm, "end": v(-33, 90) * mm});
            skLineSegment(sketch, "E86", {"start": v(-33, 90) * mm, "end": v(33, 90) * mm});
            skLineSegment(sketch, "E87", {"start": v(-80, 0) * mm, "end": v(80, 0) * mm, "construction": true});
            skLineSegment(sketch, "E88.MirrorCS", {"start": v(-15, -108) * mm, "end": v(-33, -90) * mm});
            skLineSegment(sketch, "E89.MirrorCS", {"start": v(-15, -120) * mm, "end": v(-15, -108) * mm});
            skArc(sketch, "E90.MirrorCS", {"start": v(15, -120) * mm, "mid": v(0, -135) * mm, "end": v(-15, -120) * mm});
            skLineSegment(sketch, "E91.MirrorCS", {"start": v(-33, -90) * mm, "end": v(33, -90) * mm});
            skPoint(sketch, "E92.MirrorP", {"position": v(0, -90) * mm});
            skLineSegment(sketch, "E93.MirrorCS", {"start": v(15, -108) * mm, "end": v(15, -120) * mm});
            skLineSegment(sketch, "E94.MirrorCS", {"start": v(33, -90) * mm, "end": v(15, -108) * mm});
            skCircle(sketch, "E95.MirrorC", {"center": v(0, -120) * mm, "radius": 6 * mm});
            skLineSegment(sketch, "E96.MirrorCS", {"start": v(0, -90) * mm, "end": v(0, -120) * mm, "construction": true});
            skSolve(sketch);
        }
        {
            var Q0;
            Q0=makeQuery(id+"F16.imprint","IMPRINT",FACE,{"disambiguationData":[TD([[makeQuery(id+"F16.imprint","IMPRINT",EDGE,{"derivedFrom":sQuery(id+"F16.wireOp",EDGE,"E80")}),-1.0]])]});
            var Q1;
            {var subQ5=sQuery(id+"F16.wireOp",EDGE,"E86");Q1=makeQuery(id+"F16.imprint","IMPRINT",FACE,{"disambiguationData":[TD([[makeQuery(id+"F16.imprint","IMPRINT",EDGE,{"derivedFrom":subQ5}),-1.0]])]});}
            var Q2;
            Q2=makeQuery(id+"F16.imprint","IMPRINT",FACE,{"disambiguationData":[TD([[makeQuery(id+"F16.imprint","IMPRINT",EDGE,{"derivedFrom":sQuery(id+"F16.wireOp",EDGE,"E88.MirrorCS")}),-1.0]])]});
            var Q3;
            Q3=makeQuery(id+"F2.opExtrude","CAP_FACE",FACE,{"disambiguationData":[OSD([sQuery(id+"F0.wireOp",EDGE,"E12"),sQuery(id+"F0.wireOp",EDGE,"E13"),sQuery(id+"F0.wireOp",EDGE,"E14"),sQuery(id+"F0.wireOp",EDGE,"E15"),sQuery(id+"F0.wireOp",EDGE,"E17.filletArc"),sQuery(id+"F0.wireOp",EDGE,"E18.filletArc"),sQuery(id+"F0.wireOp",EDGE,"E19.filletArc"),sQuery(id+"F0.wireOp",EDGE,"E20.filletArc"),sQuery(id+"F0.wireOp",EDGE,"E25.0"),sQuery(id+"F0.wireOp",EDGE,"E25.1"),sQuery(id+"F0.wireOp",EDGE,"E25.2"),sQuery(id+"F0.wireOp",EDGE,"E25.3"),sQuery(id+"F0.wireOp",EDGE,"E25.4"),sQuery(id+"F0.wireOp",EDGE,"E25.5"),sQuery(id+"F0.wireOp",EDGE,"E25.6"),sQuery(id+"F0.wireOp",EDGE,"E25.7")])],"isStart":false});
            extrude(context, id + "F17", {"entities" : qUnion([Q0, Q1, Q2]), "endBound" : BoundingType.UP_TO_SURFACE, "endBoundEntityFace" : qUnion([Q3]), "depth" : 25 * mm});
        }
    });
